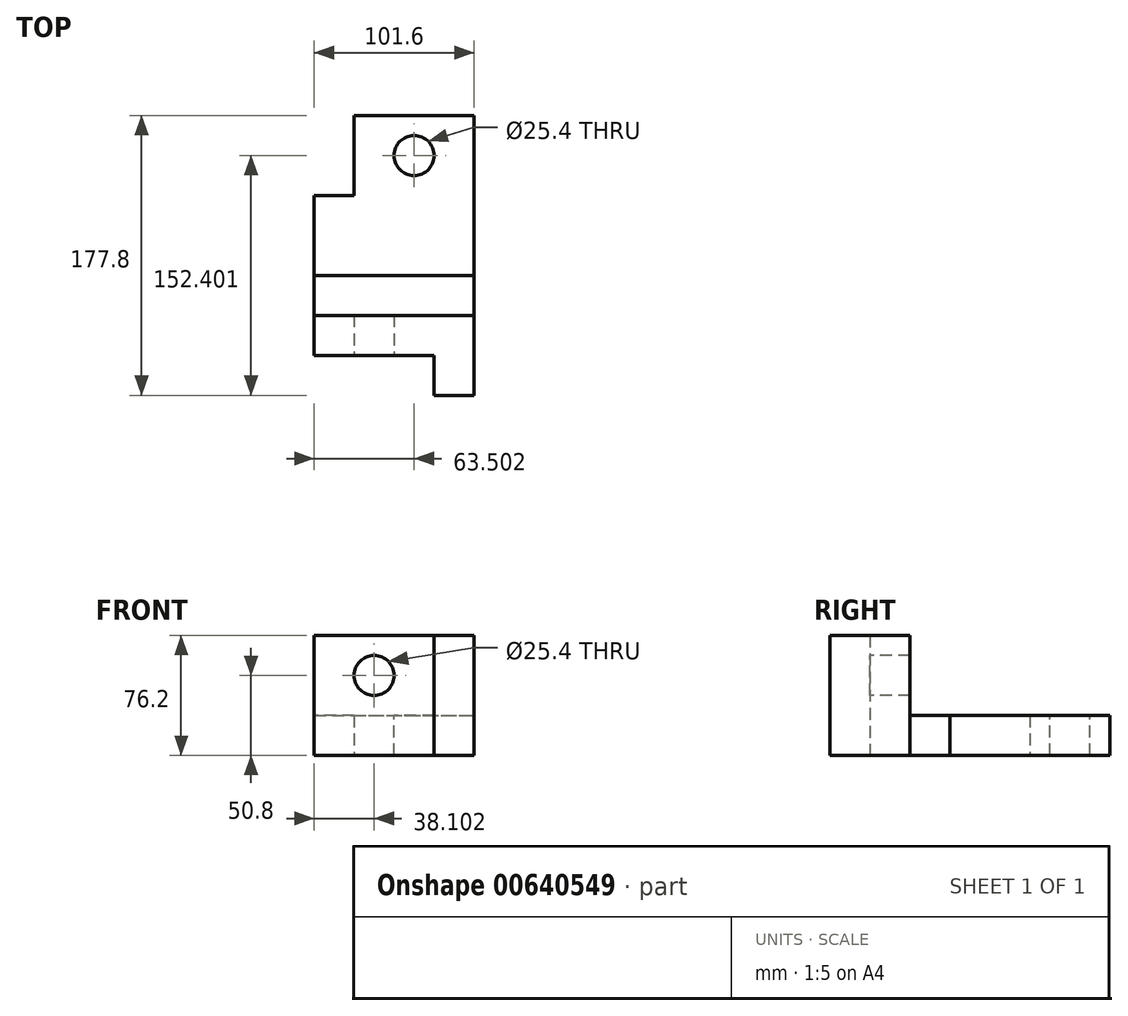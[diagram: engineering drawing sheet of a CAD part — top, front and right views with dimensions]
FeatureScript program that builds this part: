
annotation { "Feature Type Name" : "Feature", "Feature Type Description" : "" }
export const myFeature = defineFeature(function(context is Context, id is Id, definition is map)
    precondition{}
    {
        {
            var Q0;
            Q0=qCreatedBy(makeId("Top.planeOp"),FACE);
            var sketch = newSketch(context, id + "F0", { "sketchPlane" : qUnion([Q0])});
            skLineSegment(sketch, "E0.bottom", {"start": v(-73.17, 82.12) * mm, "end": v(28.43, 82.12) * mm});
            skLineSegment(sketch, "E0.top", {"start": v(-73.17, -95.68) * mm, "end": v(28.43, -95.68) * mm});
            skLineSegment(sketch, "E0.left", {"start": v(-73.17, 82.12) * mm, "end": v(-73.17, -95.68) * mm});
            skLineSegment(sketch, "E0.right", {"start": v(28.43, 82.12) * mm, "end": v(28.43, -95.68) * mm});
            skLineSegment(sketch, "E1", {"start": v(-47.77, 82.12) * mm, "end": v(-47.77, 31.32) * mm});
            skLineSegment(sketch, "E2", {"start": v(-47.77, 31.32) * mm, "end": v(-73.17, 31.32) * mm});
            skLineSegment(sketch, "E3", {"start": v(-47.77, 31.32) * mm, "end": v(-47.77, -70.28) * mm});
            skLineSegment(sketch, "E4", {"start": v(-47.77, -70.28) * mm, "end": v(-73.17, -70.28) * mm});
            skLineSegment(sketch, "E5", {"start": v(-47.77, -70.28) * mm, "end": v(3.03, -70.28) * mm});
            skLineSegment(sketch, "E6", {"start": v(3.03, -70.28) * mm, "end": v(3.03, -95.68) * mm});
            skLineSegment(sketch, "E7", {"start": v(-73.17, -19.48) * mm, "end": v(-47.77, -19.48) * mm});
            skLineSegment(sketch, "E8", {"start": v(-47.77, -19.48) * mm, "end": v(28.43, -19.48) * mm});
            skLineSegment(sketch, "E9", {"start": v(-73.17, -44.88) * mm, "end": v(28.43, -44.88) * mm});
            skSolve(sketch);
        }
        {
            var Q0;
            {var subQ1=sQuery(id+"F0.wireOp",EDGE,"E1");Q0=makeQuery(id+"F0.imprint","IMPRINT",FACE,{"disambiguationData":[TD([[makeQuery(id+"F0.imprint","IMPRINT",EDGE,{"derivedFrom":subQ1}),1.0]])]});}
            var Q1;
            {var subQ0=sQuery(id+"F0.wireOp",EDGE,"E2");Q1=makeQuery(id+"F0.imprint","IMPRINT",FACE,{"disambiguationData":[TD([[makeQuery(id+"F0.imprint","IMPRINT",EDGE,{"derivedFrom":subQ0}),1.0]])]});}
            extrude(context, id + "F1", {"entities" : qUnion([Q0, Q1]), "depth" : 25.4 * mm, "offsetDistance" : 25.4 * mm});
        }
        {
            var Q0;
            {var subQ0=sQuery(id+"F0.wireOp",EDGE,"E5");Q0=makeQuery(id+"F0.imprint","IMPRINT",FACE,{"disambiguationData":[TD([[makeQuery(id+"F0.imprint","IMPRINT",EDGE,{"derivedFrom":subQ0}),1.0]])]});}
            var Q1;
            {var subQ0=sQuery(id+"F0.wireOp",EDGE,"E4");Q1=makeQuery(id+"F0.imprint","IMPRINT",FACE,{"disambiguationData":[TD([[makeQuery(id+"F0.imprint","IMPRINT",EDGE,{"derivedFrom":subQ0}),-1.0]])]});}
            extrude(context, id + "F2", {"entities" : qUnion([Q0, Q1]), "depth" : 76.2 * mm, "offsetDistance" : 25.4 * mm});
        }
        {
            var Q0;
            {var subQ0=sQuery(id+"F0.wireOp",EDGE,"E7");Q0=makeQuery(id+"F0.imprint","IMPRINT",FACE,{"disambiguationData":[TD([[makeQuery(id+"F0.imprint","IMPRINT",EDGE,{"derivedFrom":subQ0}),-1.0]])]});}
            var Q1;
            {var subQ0=sQuery(id+"F0.wireOp",EDGE,"E8");Q1=makeQuery(id+"F0.imprint","IMPRINT",FACE,{"disambiguationData":[TD([[makeQuery(id+"F0.imprint","IMPRINT",EDGE,{"derivedFrom":subQ0}),-1.0]])]});}
            extrude(context, id + "F3", {"entities" : qUnion([Q0, Q1]), "depth" : 25.4 * mm, "offsetDistance" : 25.4 * mm});
        }
        {
            var Q0;
            Q0=makeQuery(id+"F2.opExtrude","SWEPT_FACE",FACE,{"disambiguationData":[OSD([sQuery(id+"F0.wireOp",EDGE,"E4"),sQuery(id+"F0.wireOp",EDGE,"E5")])]});
            var sketch = newSketch(context, id + "F4", { "sketchPlane" : qUnion([Q0])});
            skPoint(sketch, "E10.start.orphan", {"position": v(-35.07, 76.2) * mm});
            skCircle(sketch, "E11", {"center": v(-35.07, 50.8) * mm, "radius": 12.7 * mm});
            skSolve(sketch);
        }
        {
            var Q0;
            Q0=makeQuery(id+"F4.imprint","IMPRINT",FACE,{"disambiguationData":[TD([[makeQuery(id+"F4.imprint","IMPRINT",EDGE,{"derivedFrom":sQuery(id+"F4.wireOp",EDGE,"E11")}),1.0]])]});
            extrude(context, id + "F5", {"entities" : qUnion([Q0]), "operationType" : NewBodyOperationType.REMOVE, "oppositeDirection" : true, "depth" : 25.4 * mm, "offsetDistance" : 25.4 * mm});
        }
        {
            var Q0;
            Q0=makeQuery(id+"F1.opExtrude","CAP_FACE",FACE,{"disambiguationData":[OSD([sQuery(id+"F0.wireOp",EDGE,"E0.bottom"),sQuery(id+"F0.wireOp",EDGE,"E0.left"),sQuery(id+"F0.wireOp",EDGE,"E0.right"),sQuery(id+"F0.wireOp",EDGE,"E1"),sQuery(id+"F0.wireOp",EDGE,"E2"),sQuery(id+"F0.wireOp",EDGE,"E7"),sQuery(id+"F0.wireOp",EDGE,"E8")])],"isStart":false});
            var sketch = newSketch(context, id + "F6", { "sketchPlane" : qUnion([Q0])});
            skCircle(sketch, "E12", {"center": v(-9.67, 56.72) * mm, "radius": 12.7 * mm});
            skPoint(sketch, "E12.centerSnap0", {"position": v(-9.67, 82.12) * mm});
            skSolve(sketch);
        }
        {
            var Q0;
            Q0=makeQuery(id+"F6.imprint","IMPRINT",FACE,{"disambiguationData":[TD([[makeQuery(id+"F6.imprint","IMPRINT",EDGE,{"derivedFrom":sQuery(id+"F6.wireOp",EDGE,"E12")}),1.0]])]});
            extrude(context, id + "F7", {"entities" : qUnion([Q0]), "operationType" : NewBodyOperationType.REMOVE, "oppositeDirection" : true, "depth" : 25.4 * mm, "offsetDistance" : 25.4 * mm});
        }
    });
